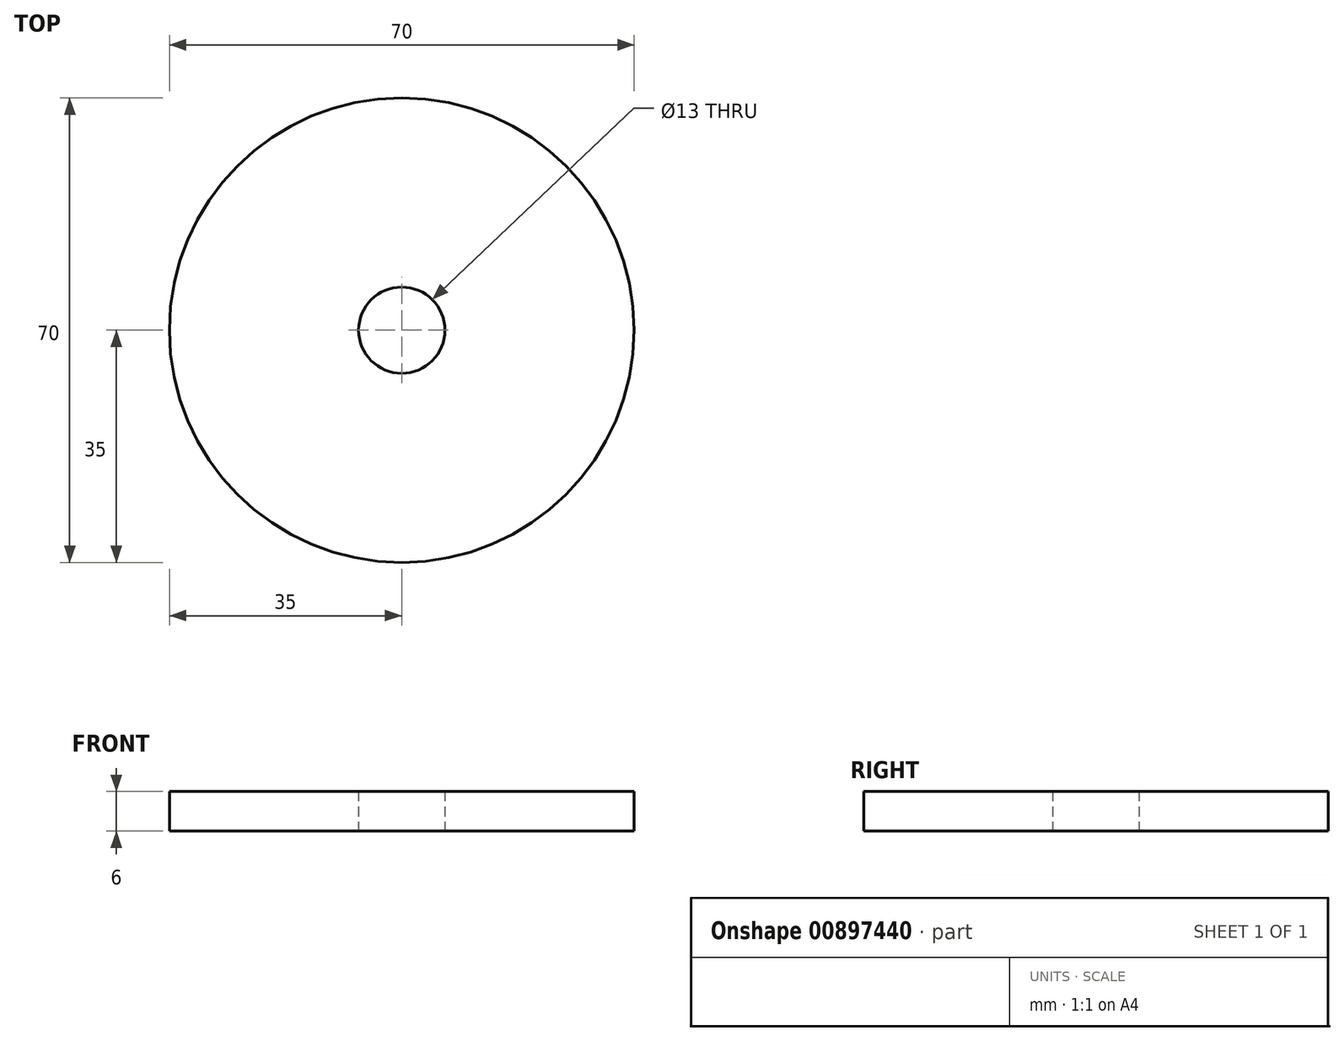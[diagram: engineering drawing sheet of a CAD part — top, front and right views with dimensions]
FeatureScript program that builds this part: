
annotation { "Feature Type Name" : "Feature", "Feature Type Description" : "" }
export const myFeature = defineFeature(function(context is Context, id is Id, definition is map)
    precondition{}
    {
        {
            var Q0;
            Q0=qCreatedBy(makeId("Top.planeOp"),FACE);
            var sketch = newSketch(context, id + "F0", { "sketchPlane" : qUnion([Q0])});
            skCircle(sketch, "E0", {"center": v(0, 0) * mm, "radius": 35 * mm});
            skCircle(sketch, "E1", {"center": v(0, 0) * mm, "radius": 6.5 * mm});
            skSolve(sketch);
        }
        {
            var Q0;
            Q0=makeQuery(id+"F0.imprint","IMPRINT",FACE,{"disambiguationData":[TD([[makeQuery(id+"F0.imprint","IMPRINT",EDGE,{"derivedFrom":sQuery(id+"F0.wireOp",EDGE,"E0")}),1.0]])]});
            extrude(context, id + "F1", {"entities" : qUnion([Q0]), "depth" : 6 * mm, "offsetDistance" : 25 * mm});
        }
    });
